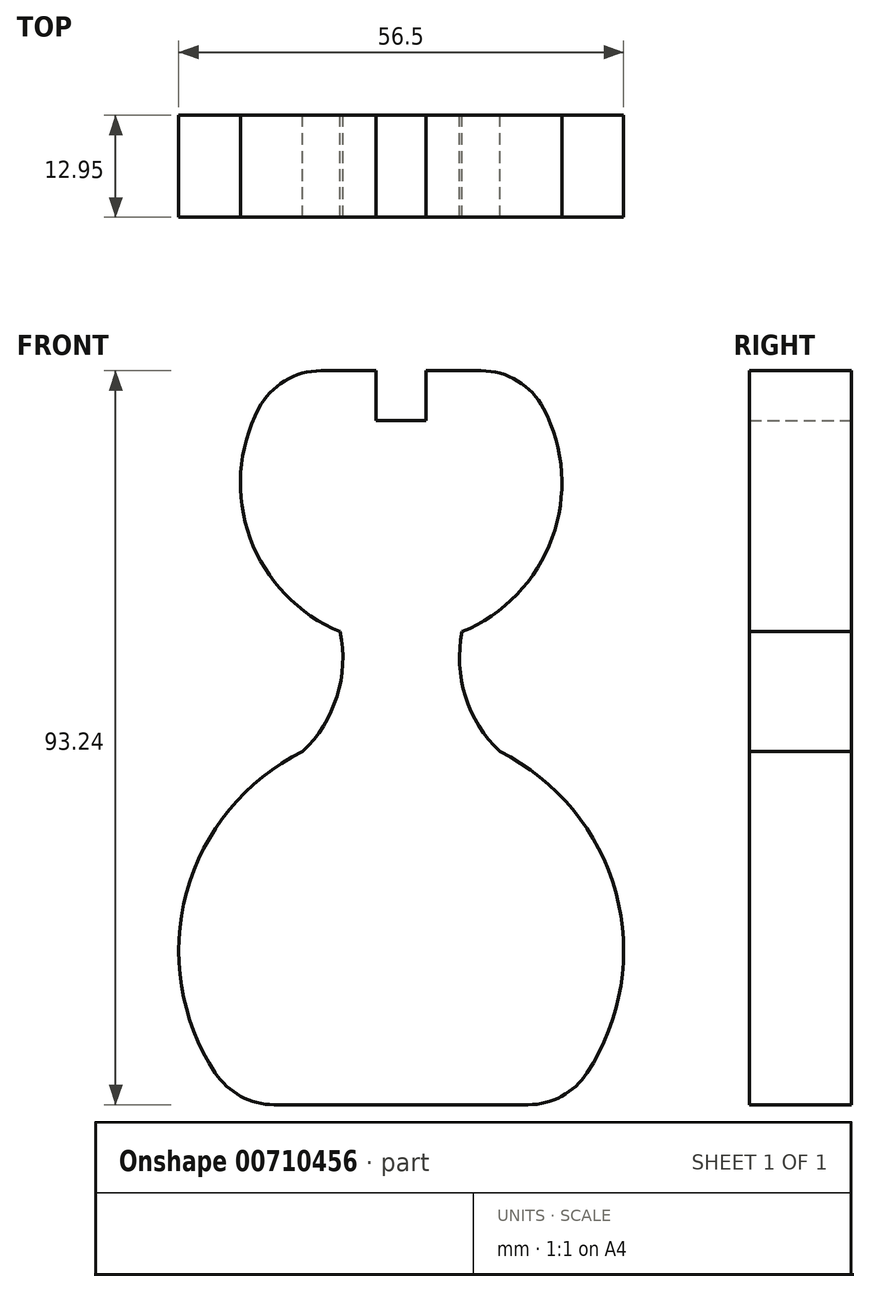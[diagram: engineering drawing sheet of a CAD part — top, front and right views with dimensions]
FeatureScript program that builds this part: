
annotation { "Feature Type Name" : "Feature", "Feature Type Description" : "" }
export const myFeature = defineFeature(function(context is Context, id is Id, definition is map)
    precondition{}
    {
        {
            var Q0;
            Q0=qCreatedBy(makeId("Top.planeOp"),FACE);
            var sketch = newSketch(context, id + "F0", { "sketchPlane" : qUnion([Q0])});
            skArc(sketch, "E0", {"start": v(20.4, -25.2) * mm, "mid": v(0, 22.58) * mm, "end": v(-20.4, -25.2) * mm});
            skArc(sketch, "E1", {"start": v(-17.7, 16.34) * mm, "mid": v(-9.36, 23.8) * mm, "end": v(-7.74, 34.88) * mm});
            skArc(sketch, "E2.MirrorC", {"start": v(17.7, 16.34) * mm, "mid": v(9.36, 23.8) * mm, "end": v(7.74, 34.88) * mm});
            skArc(sketch, "E3", {"start": v(-14.6, 68.04) * mm, "mid": v(0, 33.35) * mm, "end": v(14.6, 68.04) * mm});
            skLineSegment(sketch, "E4", {"start": v(-14.6, 68.04) * mm, "end": v(-3.18, 68.04) * mm});
            skLineSegment(sketch, "E5", {"start": v(3.18, 68.04) * mm, "end": v(3.18, 61.7) * mm});
            skLineSegment(sketch, "E6", {"start": v(3.18, 61.7) * mm, "end": v(-3.18, 61.7) * mm});
            skLineSegment(sketch, "E7", {"start": v(-3.18, 61.7) * mm, "end": v(-3.18, 68.04) * mm});
            skPoint(sketch, "E7.endSnap0", {"position": v(0, 68.04) * mm});
            skLineSegment(sketch, "E8.trimOffspring", {"start": v(3.18, 68.04) * mm, "end": v(14.6, 68.04) * mm});
            skPoint(sketch, "E9.end.orphan", {"position": v(3.18, 63.06) * mm});
            skPoint(sketch, "E9.start.orphan", {"position": v(0, 63.06) * mm});
            skLineSegment(sketch, "E10", {"start": v(-20.4, -25.2) * mm, "end": v(20.4, -25.2) * mm});
            skPoint(sketch, "E11", {"position": v(0, 12.97) * mm});
            skSolve(sketch);
        }
        {
            var Q0;
            Q0 = qSketchRegion(id + "F0", true);
            extrude(context, id + "F1", {"entities" : qUnion([Q0]), "depth" : 12.95 * mm, "offsetDistance" : 25.4 * mm});
        }
        {
            var Q0;
            Q0=makeQuery(id+"F1.opExtrude","SWEPT_EDGE",EDGE,{"disambiguationData":[OSD([sQuery(id+"F0.wireOp",EDGE,"E3"),sQuery(id+"F0.wireOp",EDGE,"E8.trimOffspring")])]});
            var Q1;
            Q1=makeQuery(id+"F1.opExtrude","SWEPT_EDGE",EDGE,{"disambiguationData":[OSD([sQuery(id+"F0.wireOp",EDGE,"E3"),sQuery(id+"F0.wireOp",EDGE,"E4")])]});
            var Q2;
            {var subQ0=sQuery(id+"F0.wireOp",EDGE,"E10");var subQ1=sQuery(id+"F0.wireOp",EDGE,"E0");Q2=makeQuery(id+"F1.opExtrude","SWEPT_EDGE",EDGE,{"disambiguationData":[OSD([subQ1,subQ0]),TDD([makeQuery(id+"F0.imprint","INTERSECT",VERTEX,{"disambiguationData":[OD(1.0)],"derivedFrom":[subQ1,subQ0]})])]});}
            var Q3;
            {var subQ0=sQuery(id+"F0.wireOp",EDGE,"E10");var subQ1=sQuery(id+"F0.wireOp",EDGE,"E0");Q3=makeQuery(id+"F1.opExtrude","SWEPT_EDGE",EDGE,{"disambiguationData":[OSD([subQ1,subQ0]),TDD([makeQuery(id+"F0.imprint","INTERSECT",VERTEX,{"disambiguationData":[OD(0.0)],"derivedFrom":[subQ1,subQ0]})])]});}
            fillet(context, id + "F2", {"entities" : qUnion([Q0, Q1, Q2, Q3]), "radius" : 8.96 * mm, "tangentPropagation" : true, "allowEdgeOverflow" : false});
        }
        {
            var Q0;
            Q0=makeQuery(id+"F1.opExtrude","SWEPT_BODY",BODY,{"disambiguationData":[OSD([sQuery(id+"F0.wireOp",EDGE,"E0"),sQuery(id+"F0.wireOp",EDGE,"E1"),sQuery(id+"F0.wireOp",EDGE,"E2.MirrorC"),sQuery(id+"F0.wireOp",EDGE,"E3"),sQuery(id+"F0.wireOp",EDGE,"E4"),sQuery(id+"F0.wireOp",EDGE,"E5"),sQuery(id+"F0.wireOp",EDGE,"E6"),sQuery(id+"F0.wireOp",EDGE,"E7"),sQuery(id+"F0.wireOp",EDGE,"E8.trimOffspring"),sQuery(id+"F0.wireOp",EDGE,"E10")])]});
            var Q1;
            Q1=makeQuery(id+"F1.opExtrude","CAP_EDGE",EDGE,{"disambiguationData":[OSD([sQuery(id+"F0.wireOp",EDGE,"E10")])],"isStart":true});
            transform(context, id + "F3", {"entities" : qUnion([Q0]), "transformType" : TransformType.ROTATION, "transformAxis" : qUnion([Q1]), "angle" : 90 * degree, "makeCopy" : false});
        }
    });
